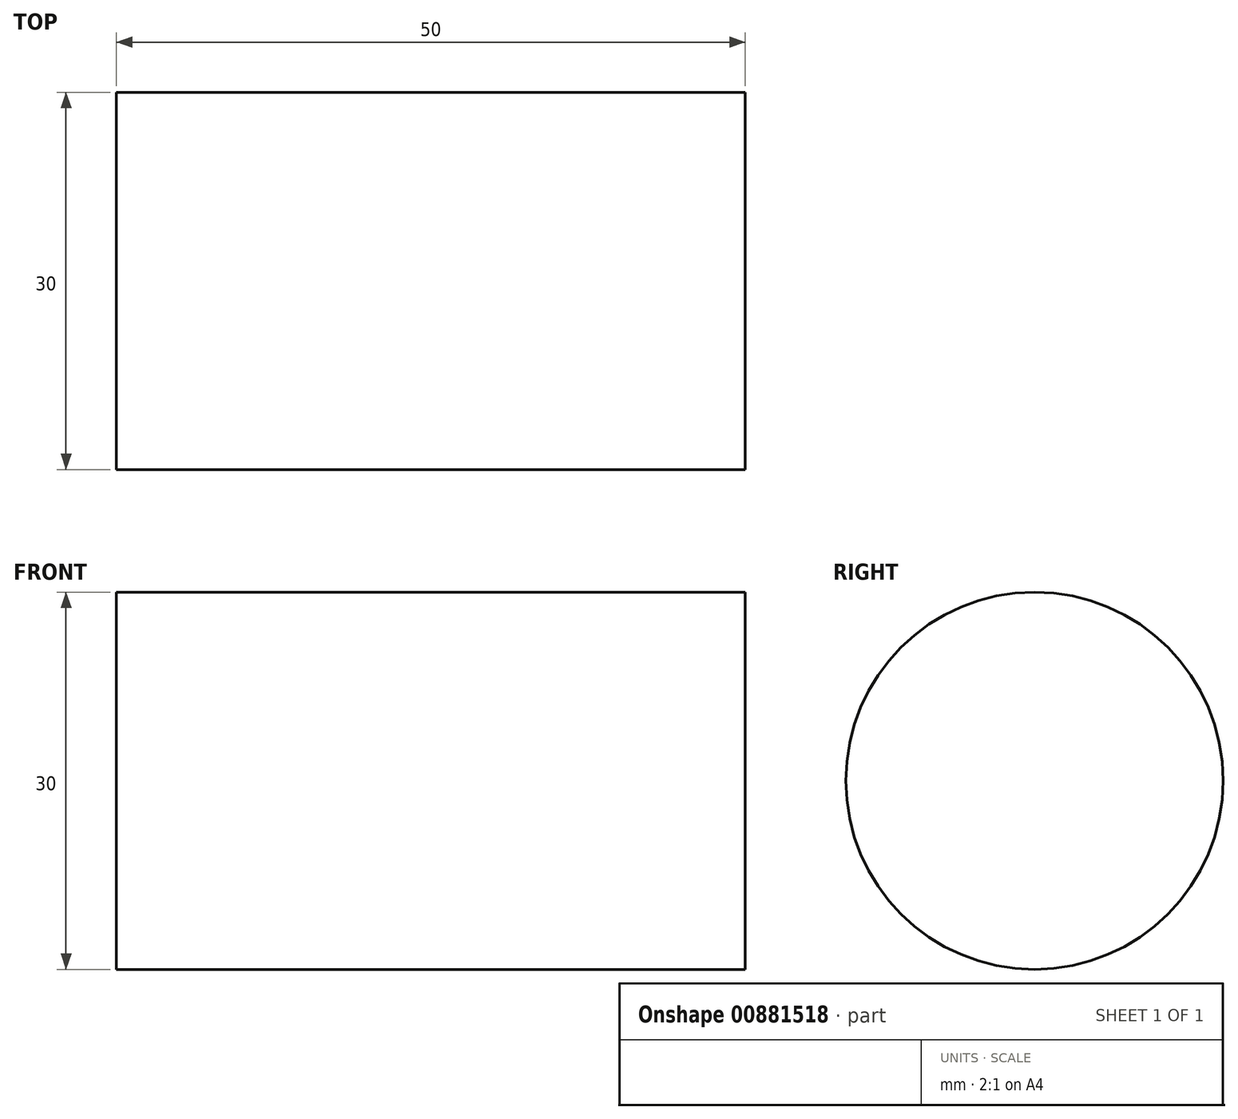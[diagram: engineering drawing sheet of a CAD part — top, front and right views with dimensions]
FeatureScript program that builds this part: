
annotation { "Feature Type Name" : "Feature", "Feature Type Description" : "" }
export const myFeature = defineFeature(function(context is Context, id is Id, definition is map)
    precondition{}
    {
        {
            var Q0;
            Q0=qCreatedBy(makeId("Front.planeOp"),FACE);
            var sketch = newSketch(context, id + "F0", { "sketchPlane" : qUnion([Q0])});
            skLineSegment(sketch, "E0.bottom", {"start": v(100, 12.5) * mm, "end": v(-100, 12.5) * mm});
            skLineSegment(sketch, "E0.top", {"start": v(100, -12.5) * mm, "end": v(-100, -12.5) * mm});
            skLineSegment(sketch, "E0.left", {"start": v(100, 12.5) * mm, "end": v(100, -12.5) * mm});
            skLineSegment(sketch, "E0.right", {"start": v(-100, 12.5) * mm, "end": v(-100, -12.5) * mm});
            skPoint(sketch, "E0.middle", {"position": v(0, 0) * mm});
            skSolve(sketch);
        }
        {
            var Q0;
            Q0=qCreatedBy(makeId("Right.planeOp"),FACE);
            var Q1;
            Q1=qCreatedBy(makeId("Right.planeOp"),FACE);
            var Q2;
            Q2=qCreatedBy(makeId("Front.planeOp"),FACE);
            var Q3;
            Q3=qCreatedBy(makeId("Right.planeOp"),FACE);
            var sketch = newSketch(context, id + "F1", { "sketchPlane" : qUnion([Q0, Q1, Q2, Q3])});
            skCircle(sketch, "E1", {"center": v(0, 0) * mm, "radius": 15 * mm});
            skSolve(sketch);
        }
        {
            var Q0;
            Q0=makeQuery(id+"F1.imprint","IMPRINT",FACE,{"disambiguationData":[TD([[makeQuery(id+"F1.imprint","IMPRINT",EDGE,{"derivedFrom":sQuery(id+"F1.wireOp",EDGE,"E1")}),1.0]])]});
            extrude(context, id + "F2", {"entities" : qUnion([Q0]), "depth" : 50 * mm, "offsetDistance" : 25 * mm});
        }
    });
